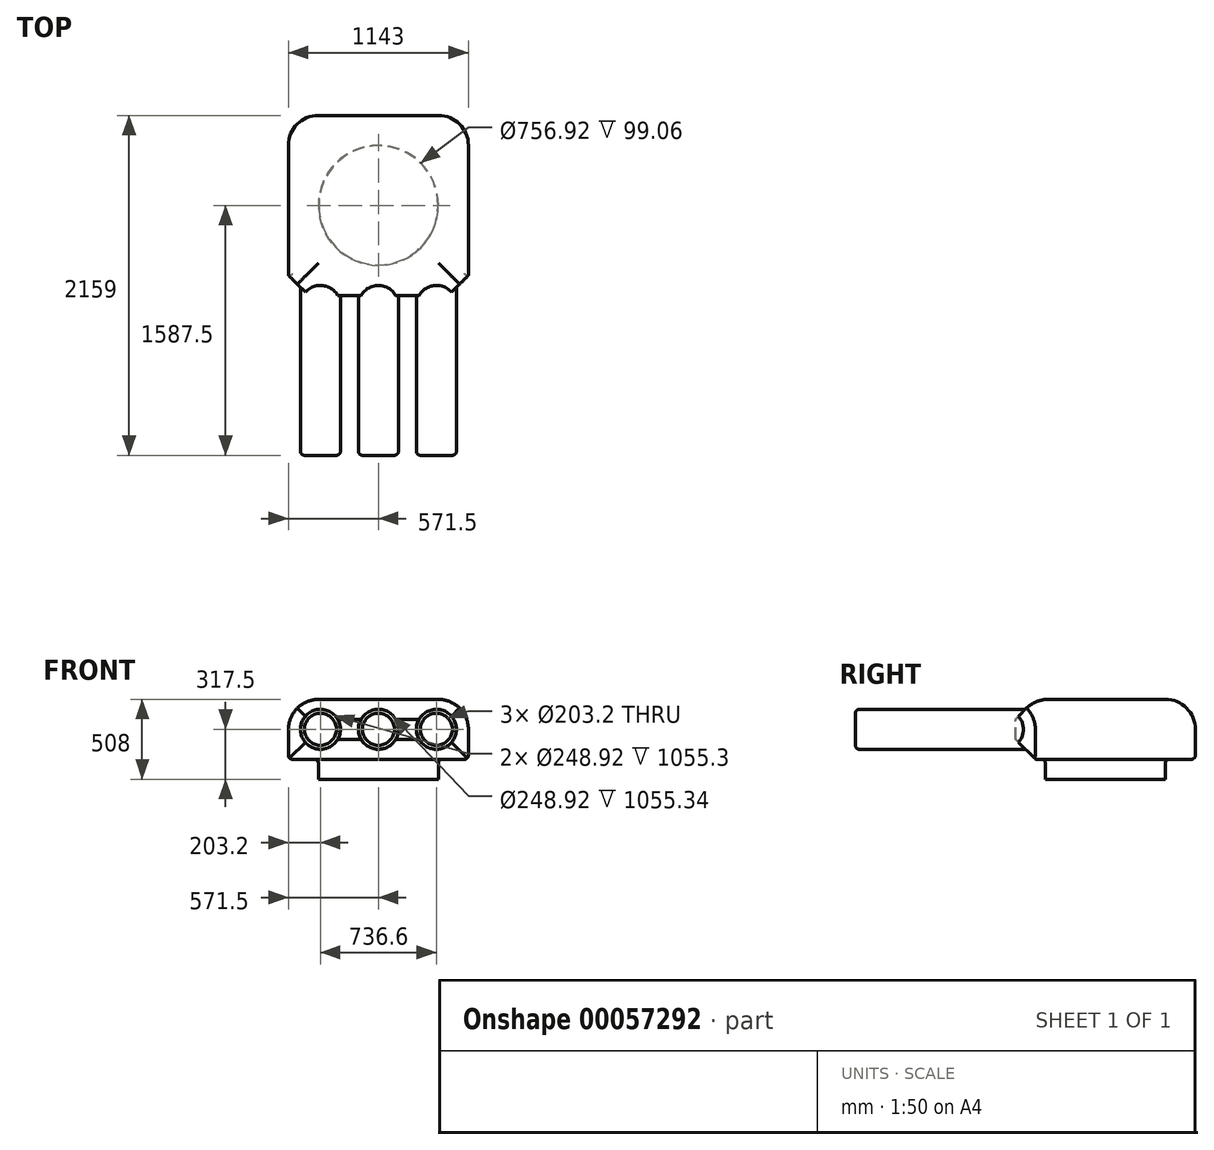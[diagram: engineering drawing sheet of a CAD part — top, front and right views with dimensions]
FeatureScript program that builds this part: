
annotation { "Feature Type Name" : "Feature", "Feature Type Description" : "" }
export const myFeature = defineFeature(function(context is Context, id is Id, definition is map)
    precondition{}
    {
        {
            var Q0;
            Q0=qCreatedBy(makeId("Top.planeOp"),FACE);
            var sketch = newSketch(context, id + "F0", { "sketchPlane" : qUnion([Q0])});
            skCircle(sketch, "E0", {"center": v(0, 0) * mm, "radius": 381 * mm});
            skSolve(sketch);
        }
        {
            var Q0;
            Q0=makeQuery(id+"F0.imprint","IMPRINT",FACE,{"disambiguationData":[TD([[makeQuery(id+"F0.imprint","IMPRINT",EDGE,{"derivedFrom":sQuery(id+"F0.wireOp",EDGE,"E0")}),1.0]])]});
            extrude(context, id + "F1", {"entities" : qUnion([Q0]), "depth" : 127 * mm});
        }
        {
            var Q0;
            Q0=makeQuery(id+"F1.opExtrude","CAP_FACE",FACE,{"disambiguationData":[OSD([sQuery(id+"F0.wireOp",EDGE,"E0")])],"isStart":false});
            var sketch = newSketch(context, id + "F2", { "sketchPlane" : qUnion([Q0])});
            skLineSegment(sketch, "E1.rect.bottom", {"start": v(571.5, -571.5) * mm, "end": v(-571.5, -571.5) * mm});
            skLineSegment(sketch, "E1.rect.top", {"start": v(571.5, 571.5) * mm, "end": v(-571.5, 571.5) * mm});
            skLineSegment(sketch, "E1.rect.left", {"start": v(571.5, -571.5) * mm, "end": v(571.5, 571.5) * mm});
            skLineSegment(sketch, "E1.rect.right", {"start": v(-571.5, -571.5) * mm, "end": v(-571.5, 571.5) * mm});
            skPoint(sketch, "E1.rect.middle", {"position": v(0, 0) * mm});
            skSolve(sketch);
        }
        {
            var Q0;
            Q0=makeQuery(id+"F2.imprint","IMPRINT",FACE,{"disambiguationData":[TD([[makeQuery(id+"F2.imprint","IMPRINT",EDGE,{"derivedFrom":sQuery(id+"F2.wireOp",EDGE,"E1.rect.bottom")}),-1.0]])]});
            var Q1;
            Q1=makeQuery(id+"F2.imprint","IMPRINT",FACE,{"disambiguationData":[TD([[makeQuery(id+"F2.imprint","IMPRINT",EDGE,{"derivedFrom":makeQuery(id+"F1.opExtrude","CAP_EDGE",EDGE,{"disambiguationData":[OSD([sQuery(id+"F0.wireOp",EDGE,"E0")])],"isStart":false})}),1.0]])]});
            extrude(context, id + "F3", {"entities" : qUnion([Q0, Q1]), "operationType" : NewBodyOperationType.ADD, "depth" : 381 * mm});
        }
        {
            var Q0;
            Q0=makeQuery(id+"F3.opExtrude","SWEPT_FACE",FACE,{"disambiguationData":[OSD([sQuery(id+"F2.wireOp",EDGE,"E1.rect.bottom")])]});
            var sketch = newSketch(context, id + "F4", { "sketchPlane" : qUnion([Q0])});
            skCircle(sketch, "E2", {"center": v(0, 317.5) * mm, "radius": 127 * mm});
            skPoint(sketch, "E2.centerSnap0", {"position": v(-571.5, 317.5) * mm});
            skCircle(sketch, "E3", {"center": v(-368.3, 317.5) * mm, "radius": 127 * mm});
            skCircle(sketch, "E4", {"center": v(368.3, 317.5) * mm, "radius": 127 * mm});
            skPoint(sketch, "E4.centerSnap0", {"position": v(571.5, 317.5) * mm});
            skSolve(sketch);
        }
        {
            var Q0;
            Q0=makeQuery(id+"F4.imprint","IMPRINT",FACE,{"disambiguationData":[TD([[makeQuery(id+"F4.imprint","IMPRINT",EDGE,{"derivedFrom":sQuery(id+"F4.wireOp",EDGE,"E3")}),1.0]])]});
            var Q1;
            Q1=makeQuery(id+"F4.imprint","IMPRINT",FACE,{"disambiguationData":[TD([[makeQuery(id+"F4.imprint","IMPRINT",EDGE,{"derivedFrom":sQuery(id+"F4.wireOp",EDGE,"E2")}),1.0]])]});
            var Q2;
            Q2=makeQuery(id+"F4.imprint","IMPRINT",FACE,{"disambiguationData":[TD([[makeQuery(id+"F4.imprint","IMPRINT",EDGE,{"derivedFrom":sQuery(id+"F4.wireOp",EDGE,"E4")}),1.0]])]});
            extrude(context, id + "F5", {"entities" : qUnion([Q0, Q1, Q2]), "operationType" : NewBodyOperationType.ADD, "depth" : 1016 * mm});
        }
        {
            var Q0;
            Q0=makeQuery(id+"F3.opExtrude","CAP_EDGE",EDGE,{"disambiguationData":[OSD([sQuery(id+"F2.wireOp",EDGE,"E1.rect.bottom")])],"isStart":false});
            var Q1;
            Q1=makeQuery(id+"F3.opExtrude","CAP_EDGE",EDGE,{"disambiguationData":[OSD([sQuery(id+"F2.wireOp",EDGE,"E1.rect.bottom")])],"isStart":true});
            var Q2;
            Q2=makeQuery(id+"F3.opExtrude","SWEPT_EDGE",EDGE,{"disambiguationData":[OSD([sQuery(id+"F2.wireOp",EDGE,"E1.rect.bottom"),sQuery(id+"F2.wireOp",EDGE,"E1.rect.right")])]});
            var Q3;
            Q3=makeQuery(id+"F3.opExtrude","SWEPT_EDGE",EDGE,{"disambiguationData":[OSD([sQuery(id+"F2.wireOp",EDGE,"E1.rect.bottom"),sQuery(id+"F2.wireOp",EDGE,"E1.rect.left")])]});
            chamfer(context, id + "F6", {"entities" : qUnion([Q0, Q1, Q2, Q3]), "width" : 127 * mm, "tangentPropagation" : true});
        }
        {
            var Q0;
            Q0=makeQuery(id+"F3.opExtrude","CAP_FACE",FACE,{"disambiguationData":[OSD([sQuery(id+"F2.wireOp",EDGE,"E1.rect.bottom"),sQuery(id+"F2.wireOp",EDGE,"E1.rect.top"),sQuery(id+"F2.wireOp",EDGE,"E1.rect.left"),sQuery(id+"F2.wireOp",EDGE,"E1.rect.right")])],"isStart":false});
            var Q1;
            Q1=makeQuery(id+"F3.opExtrude","SWEPT_EDGE",EDGE,{"disambiguationData":[OSD([sQuery(id+"F2.wireOp",EDGE,"E1.rect.top"),sQuery(id+"F2.wireOp",EDGE,"E1.rect.left")])]});
            var Q2;
            Q2=makeQuery(id+"F3.opExtrude","SWEPT_EDGE",EDGE,{"disambiguationData":[OSD([sQuery(id+"F2.wireOp",EDGE,"E1.rect.top"),sQuery(id+"F2.wireOp",EDGE,"E1.rect.right")])]});
            fillet(context, id + "F7", {"entities" : qUnion([Q0, Q1, Q2]), "radius" : 190.5 * mm, "tangentPropagation" : true, "allowEdgeOverflow" : false});
        }
        {
            var Q0;
            Q0=makeQuery(id+"F3.opExtrude","CAP_FACE",FACE,{"disambiguationData":[OSD([sQuery(id+"F2.wireOp",EDGE,"E1.rect.bottom"),sQuery(id+"F2.wireOp",EDGE,"E1.rect.top"),sQuery(id+"F2.wireOp",EDGE,"E1.rect.left"),sQuery(id+"F2.wireOp",EDGE,"E1.rect.right")])],"isStart":true});
            fillet(context, id + "F8", {"entities" : qUnion([Q0]), "radius" : 25.4 * mm, "tangentPropagation" : true, "allowEdgeOverflow" : false});
        }
        {
            var Q0;
            Q0=makeQuery(id+"F5.opExtrude","CAP_EDGE",EDGE,{"disambiguationData":[OSD([sQuery(id+"F4.wireOp",EDGE,"E3")])],"isStart":false});
            var Q1;
            Q1=makeQuery(id+"F5.opExtrude","CAP_EDGE",EDGE,{"disambiguationData":[OSD([sQuery(id+"F4.wireOp",EDGE,"E2")])],"isStart":false});
            var Q2;
            Q2=makeQuery(id+"F5.opExtrude","CAP_EDGE",EDGE,{"disambiguationData":[OSD([sQuery(id+"F4.wireOp",EDGE,"E4")])],"isStart":false});
            fillet(context, id + "F9", {"entities" : qUnion([Q0, Q1, Q2]), "radius" : 25.4 * mm, "tangentPropagation" : true, "allowEdgeOverflow" : false});
        }
        {
            var Q0;
            Q0=makeQuery(id+"F5.opExtrude","CAP_FACE",FACE,{"disambiguationData":[OSD([sQuery(id+"F4.wireOp",EDGE,"E3")])],"isStart":false});
            var Q1;
            Q1=makeQuery(id+"F5.opExtrude","CAP_FACE",FACE,{"disambiguationData":[OSD([sQuery(id+"F4.wireOp",EDGE,"E2")])],"isStart":false});
            var Q2;
            Q2=makeQuery(id+"F5.opExtrude","CAP_FACE",FACE,{"disambiguationData":[OSD([sQuery(id+"F4.wireOp",EDGE,"E4")])],"isStart":false});
            shell(context, id + "F10", {"entities" : qUnion([Q0, Q1, Q2]), "thickness" : 2.54 * mm});
        }
    });
